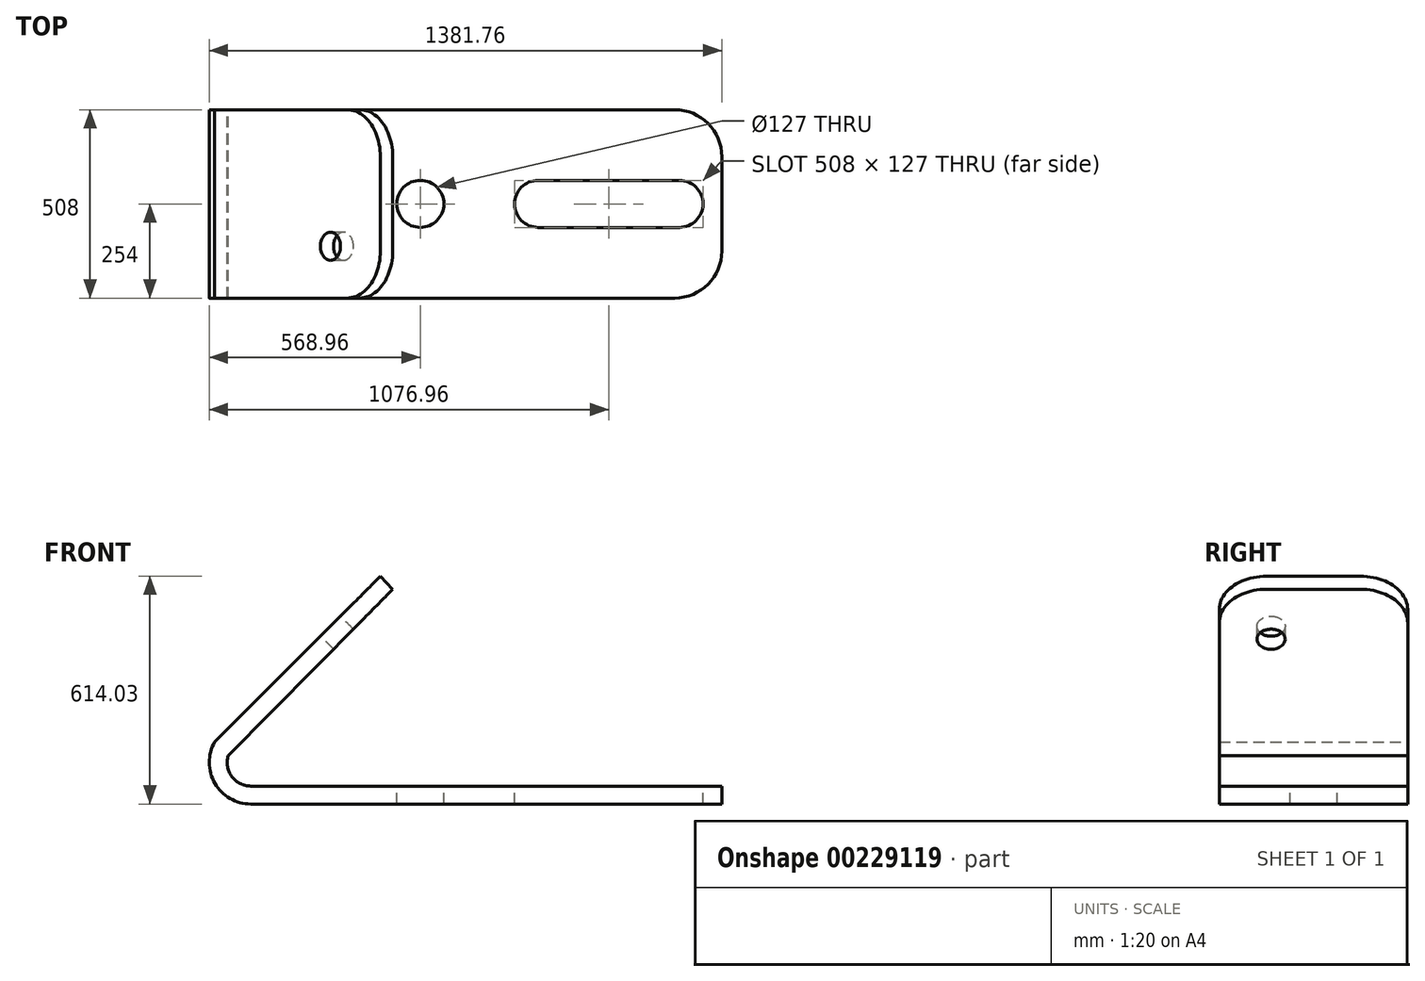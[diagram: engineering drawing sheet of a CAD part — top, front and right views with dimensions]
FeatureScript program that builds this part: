
annotation { "Feature Type Name" : "Feature", "Feature Type Description" : "" }
export const myFeature = defineFeature(function(context is Context, id is Id, definition is map)
    precondition{}
    {
        {
            var Q0;
            Q0=qCreatedBy(makeId("Front.planeOp"),FACE);
            var sketch = newSketch(context, id + "F0", { "sketchPlane" : qUnion([Q0])});
            skLineSegment(sketch, "E0", {"start": v(0, -63.5) * mm, "end": v(1270, -63.5) * mm});
            skLineSegment(sketch, "E1", {"start": v(1270, -63.5) * mm, "end": v(1270, -111.76) * mm});
            skLineSegment(sketch, "E2", {"start": v(1270, -111.76) * mm, "end": v(0, -111.76) * mm});
            skLineSegment(sketch, "E3", {"start": v(-96.97, 55.56) * mm, "end": v(349.74, 502.27) * mm});
            skLineSegment(sketch, "E4", {"start": v(-60.92, 17.92) * mm, "end": v(383.05, 467.35) * mm});
            skArc(sketch, "E5", {"start": v(-96.97, 55.56) * mm, "mid": v(-96.7, -56.04) * mm, "end": v(0, -111.76) * mm});
            skArc(sketch, "E6", {"start": v(-60.92, 17.92) * mm, "mid": v(-50.84, -38.04) * mm, "end": v(0, -63.5) * mm});
            skLineSegment(sketch, "E7", {"start": v(349.74, 502.27) * mm, "end": v(383.05, 467.35) * mm});
            skLineSegment(sketch, "E8", {"start": v(0, -111.76) * mm, "end": v(-111.76, -111.76) * mm, "construction": true});
            skLineSegment(sketch, "E9", {"start": v(-111.76, 0) * mm, "end": v(-111.76, -111.76) * mm, "construction": true});
            skSolve(sketch);
        }
        {
            var Q0;
            Q0 = qSketchRegion(id + "F0", true);
            extrude(context, id + "F1", {"entities" : qUnion([Q0]), "endBound" : BoundingType.SYMMETRIC, "depth" : 508 * mm});
        }
        {
            var Q0;
            Q0=makeQuery(id+"F1.opExtrude","SWEPT_FACE",FACE,{"disambiguationData":[OSD([sQuery(id+"F0.wireOp",EDGE,"E0")])]});
            var sketch = newSketch(context, id + "F2", { "sketchPlane" : qUnion([Q0])});
            skLineSegment(sketch, "E10", {"start": v(1270, 0) * mm, "end": v(457.2, 0) * mm, "construction": true});
            skPoint(sketch, "E10.endSnap0", {"position": v(1270, 0) * mm});
            skCircle(sketch, "E11", {"center": v(1155.7, 0) * mm, "radius": 63.5 * mm});
            skCircle(sketch, "E12", {"center": v(774.7, 0) * mm, "radius": 63.5 * mm});
            skLineSegment(sketch, "E13", {"start": v(774.7, 63.5) * mm, "end": v(1155.7, 63.5) * mm});
            skLineSegment(sketch, "E14", {"start": v(774.7, -63.5) * mm, "end": v(1155.7, -63.5) * mm});
            skCircle(sketch, "E15", {"center": v(457.2, 0) * mm, "radius": 63.5 * mm});
            skSolve(sketch);
        }
        {
            var Q0;
            Q0 = qSketchRegion(id + "F2", true);
            extrude(context, id + "F3", {"entities" : qUnion([Q0]), "operationType" : NewBodyOperationType.REMOVE, "endBound" : BoundingType.THROUGH_ALL, "oppositeDirection" : true, "depth" : 25.4 * mm});
        }
        {
            var Q0;
            Q0=makeQuery(id+"F1.opExtrude","SWEPT_FACE",FACE,{"disambiguationData":[OSD([sQuery(id+"F0.wireOp",EDGE,"E3")])]});
            var sketch = newSketch(context, id + "F4", { "sketchPlane" : qUnion([Q0])});
            skLineSegment(sketch, "E16", {"start": v(0, 602.46) * mm, "end": v(0, 411.96) * mm, "construction": true});
            skPoint(sketch, "E16.endSnap0", {"position": v(0, 602.46) * mm});
            skLineSegment(sketch, "E17", {"start": v(0, 411.96) * mm, "end": v(114.3, 411.96) * mm, "construction": true});
            skCircle(sketch, "E18", {"center": v(114.3, 411.96) * mm, "radius": 38.1 * mm});
            skSolve(sketch);
        }
        {
            var Q0;
            Q0 = qSketchRegion(id + "F4", true);
            extrude(context, id + "F5", {"entities" : qUnion([Q0]), "operationType" : NewBodyOperationType.REMOVE, "endBound" : BoundingType.UP_TO_NEXT, "oppositeDirection" : true, "depth" : 25.4 * mm});
        }
        {
            var Q0;
            Q0=makeQuery(id+"F1.opExtrude","CAP_EDGE",EDGE,{"disambiguationData":[OSD([sQuery(id+"F0.wireOp",EDGE,"E7")])],"isStart":true});
            var Q1;
            Q1=makeQuery(id+"F1.opExtrude","CAP_EDGE",EDGE,{"disambiguationData":[OSD([sQuery(id+"F0.wireOp",EDGE,"E7")])],"isStart":false});
            fillet(context, id + "F6", {"entities" : qUnion([Q0, Q1]), "radius" : 127 * mm, "tangentPropagation" : true, "allowEdgeOverflow" : false});
        }
        {
            var Q0;
            Q0=makeQuery(id+"F1.opExtrude","CAP_EDGE",EDGE,{"disambiguationData":[OSD([sQuery(id+"F0.wireOp",EDGE,"E1")])],"isStart":true});
            var Q1;
            Q1=makeQuery(id+"F1.opExtrude","CAP_EDGE",EDGE,{"disambiguationData":[OSD([sQuery(id+"F0.wireOp",EDGE,"E1")])],"isStart":false});
            fillet(context, id + "F7", {"entities" : qUnion([Q0, Q1]), "radius" : 127 * mm, "tangentPropagation" : true, "allowEdgeOverflow" : false});
        }
    });
